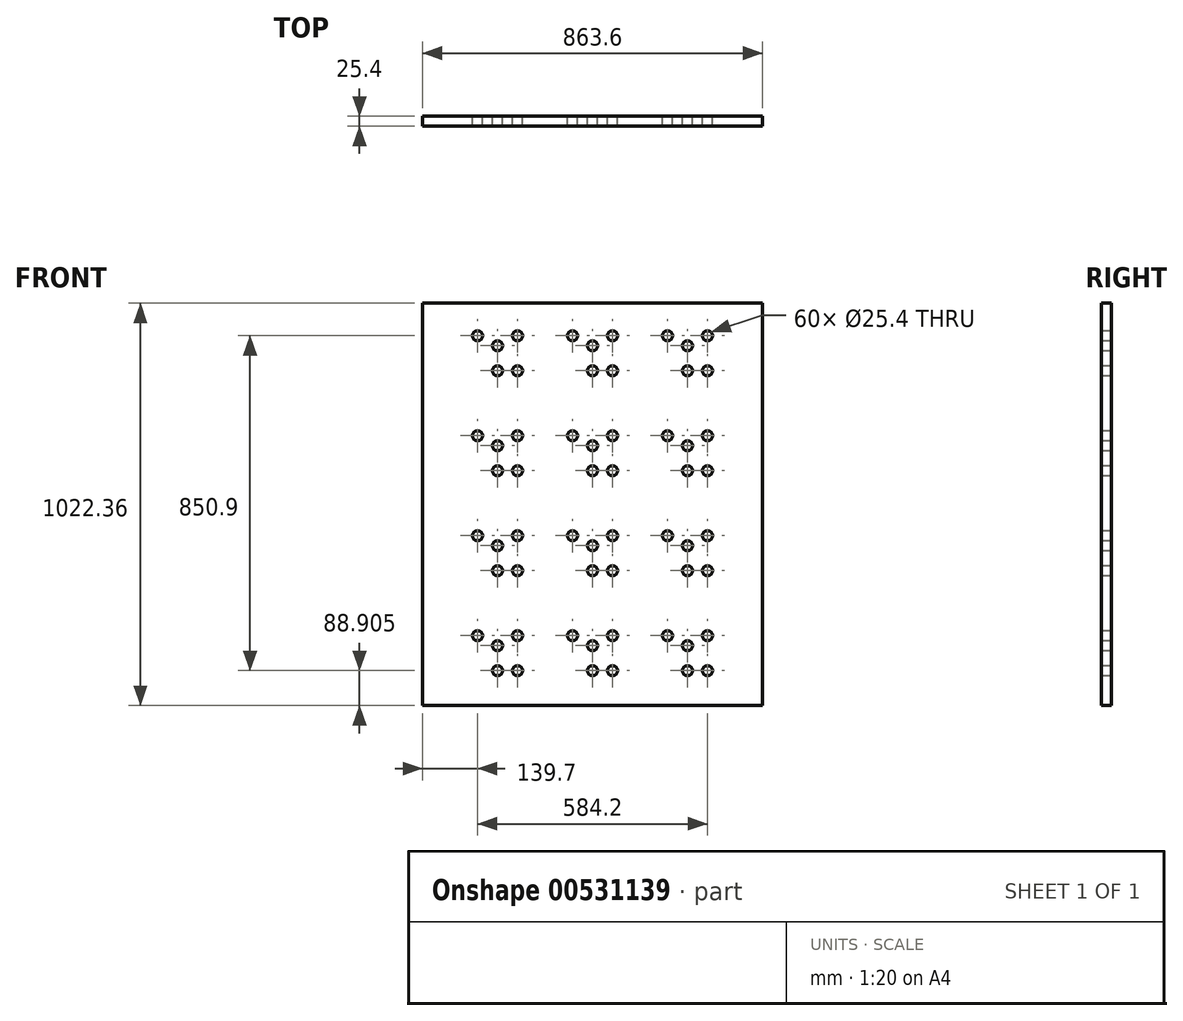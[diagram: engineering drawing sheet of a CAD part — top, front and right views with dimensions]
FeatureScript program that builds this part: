
annotation { "Feature Type Name" : "Feature", "Feature Type Description" : "" }
export const myFeature = defineFeature(function(context is Context, id is Id, definition is map)
    precondition{}
    {
        {
            var Q0;
            Q0=qCreatedBy(makeId("Front.planeOp"),FACE);
            var sketch = newSketch(context, id + "F0", { "sketchPlane" : qUnion([Q0])});
            skLineSegment(sketch, "E0.bottom", {"start": v(431.8, 511.18) * mm, "end": v(-431.8, 511.18) * mm});
            skLineSegment(sketch, "E0.top", {"start": v(431.8, -511.18) * mm, "end": v(-431.8, -511.18) * mm});
            skLineSegment(sketch, "E0.left", {"start": v(431.8, 511.18) * mm, "end": v(431.8, -511.18) * mm});
            skLineSegment(sketch, "E0.right", {"start": v(-431.8, 511.18) * mm, "end": v(-431.8, -511.18) * mm});
            skPoint(sketch, "E0.middle", {"position": v(0, 0) * mm});
            skCircle(sketch, "E1", {"center": v(-292.1, 428.63) * mm, "radius": 12.7 * mm});
            skCircle(sketch, "E2", {"center": v(-241.3, 403.23) * mm, "radius": 12.7 * mm});
            skCircle(sketch, "E3", {"center": v(-241.3, 339.73) * mm, "radius": 12.7 * mm});
            skCircle(sketch, "E4", {"center": v(-190.5, 339.73) * mm, "radius": 12.7 * mm});
            skCircle(sketch, "E5", {"center": v(-190.5, 428.63) * mm, "radius": 12.7 * mm});
            skCircle(sketch, "E6.0.1.0", {"center": v(-190.5, 85.73) * mm, "radius": 12.7 * mm});
            skCircle(sketch, "E6.0.1.1", {"center": v(-190.5, 174.63) * mm, "radius": 12.7 * mm});
            skCircle(sketch, "E6.0.1.2", {"center": v(-241.3, 149.23) * mm, "radius": 12.7 * mm});
            skCircle(sketch, "E6.0.1.3", {"center": v(-241.3, 85.73) * mm, "radius": 12.7 * mm});
            skCircle(sketch, "E6.0.1.4", {"center": v(-292.1, 174.63) * mm, "radius": 12.7 * mm});
            skCircle(sketch, "E6.0.2.0", {"center": v(-190.5, -168.27) * mm, "radius": 12.7 * mm});
            skCircle(sketch, "E6.0.2.1", {"center": v(-190.5, -79.37) * mm, "radius": 12.7 * mm});
            skCircle(sketch, "E6.0.2.2", {"center": v(-241.3, -104.77) * mm, "radius": 12.7 * mm});
            skCircle(sketch, "E6.0.2.3", {"center": v(-241.3, -168.27) * mm, "radius": 12.7 * mm});
            skCircle(sketch, "E6.0.2.4", {"center": v(-292.1, -79.37) * mm, "radius": 12.7 * mm});
            skCircle(sketch, "E6.0.3.0", {"center": v(-190.5, -422.27) * mm, "radius": 12.7 * mm});
            skCircle(sketch, "E6.0.3.1", {"center": v(-190.5, -333.38) * mm, "radius": 12.7 * mm});
            skCircle(sketch, "E6.0.3.2", {"center": v(-241.3, -358.77) * mm, "radius": 12.7 * mm});
            skCircle(sketch, "E6.0.3.3", {"center": v(-241.3, -422.27) * mm, "radius": 12.7 * mm});
            skCircle(sketch, "E6.0.3.4", {"center": v(-292.1, -333.38) * mm, "radius": 12.7 * mm});
            skCircle(sketch, "E6.1.0.0", {"center": v(50.8, 339.73) * mm, "radius": 12.7 * mm});
            skCircle(sketch, "E6.1.0.1", {"center": v(50.8, 428.63) * mm, "radius": 12.7 * mm});
            skCircle(sketch, "E6.1.0.2", {"center": v(0, 403.23) * mm, "radius": 12.7 * mm});
            skCircle(sketch, "E6.1.0.3", {"center": v(0, 339.73) * mm, "radius": 12.7 * mm});
            skCircle(sketch, "E6.1.0.4", {"center": v(-50.8, 428.63) * mm, "radius": 12.7 * mm});
            skCircle(sketch, "E6.1.1.0", {"center": v(50.8, 85.73) * mm, "radius": 12.7 * mm});
            skCircle(sketch, "E6.1.1.1", {"center": v(50.8, 174.63) * mm, "radius": 12.7 * mm});
            skCircle(sketch, "E6.1.1.2", {"center": v(0, 149.23) * mm, "radius": 12.7 * mm});
            skCircle(sketch, "E6.1.1.3", {"center": v(0, 85.73) * mm, "radius": 12.7 * mm});
            skCircle(sketch, "E6.1.1.4", {"center": v(-50.8, 174.63) * mm, "radius": 12.7 * mm});
            skCircle(sketch, "E6.1.2.0", {"center": v(50.8, -168.27) * mm, "radius": 12.7 * mm});
            skCircle(sketch, "E6.1.2.1", {"center": v(50.8, -79.37) * mm, "radius": 12.7 * mm});
            skCircle(sketch, "E6.1.2.2", {"center": v(0, -104.77) * mm, "radius": 12.7 * mm});
            skCircle(sketch, "E6.1.2.3", {"center": v(0, -168.27) * mm, "radius": 12.7 * mm});
            skCircle(sketch, "E6.1.2.4", {"center": v(-50.8, -79.37) * mm, "radius": 12.7 * mm});
            skCircle(sketch, "E6.1.3.0", {"center": v(50.8, -422.27) * mm, "radius": 12.7 * mm});
            skCircle(sketch, "E6.1.3.1", {"center": v(50.8, -333.38) * mm, "radius": 12.7 * mm});
            skCircle(sketch, "E6.1.3.2", {"center": v(0, -358.77) * mm, "radius": 12.7 * mm});
            skCircle(sketch, "E6.1.3.3", {"center": v(0, -422.27) * mm, "radius": 12.7 * mm});
            skCircle(sketch, "E6.1.3.4", {"center": v(-50.8, -333.38) * mm, "radius": 12.7 * mm});
            skCircle(sketch, "E6.2.0.0", {"center": v(292.1, 339.73) * mm, "radius": 12.7 * mm});
            skCircle(sketch, "E6.2.0.1", {"center": v(292.1, 428.63) * mm, "radius": 12.7 * mm});
            skCircle(sketch, "E6.2.0.2", {"center": v(241.3, 403.23) * mm, "radius": 12.7 * mm});
            skCircle(sketch, "E6.2.0.3", {"center": v(241.3, 339.73) * mm, "radius": 12.7 * mm});
            skCircle(sketch, "E6.2.0.4", {"center": v(190.5, 428.63) * mm, "radius": 12.7 * mm});
            skCircle(sketch, "E6.2.1.0", {"center": v(292.1, 85.73) * mm, "radius": 12.7 * mm});
            skCircle(sketch, "E6.2.1.1", {"center": v(292.1, 174.63) * mm, "radius": 12.7 * mm});
            skCircle(sketch, "E6.2.1.2", {"center": v(241.3, 149.23) * mm, "radius": 12.7 * mm});
            skCircle(sketch, "E6.2.1.3", {"center": v(241.3, 85.73) * mm, "radius": 12.7 * mm});
            skCircle(sketch, "E6.2.1.4", {"center": v(190.5, 174.63) * mm, "radius": 12.7 * mm});
            skCircle(sketch, "E6.2.2.0", {"center": v(292.1, -168.27) * mm, "radius": 12.7 * mm});
            skCircle(sketch, "E6.2.2.1", {"center": v(292.1, -79.37) * mm, "radius": 12.7 * mm});
            skCircle(sketch, "E6.2.2.2", {"center": v(241.3, -104.77) * mm, "radius": 12.7 * mm});
            skCircle(sketch, "E6.2.2.3", {"center": v(241.3, -168.27) * mm, "radius": 12.7 * mm});
            skCircle(sketch, "E6.2.2.4", {"center": v(190.5, -79.37) * mm, "radius": 12.7 * mm});
            skCircle(sketch, "E6.2.3.0", {"center": v(292.1, -422.27) * mm, "radius": 12.7 * mm});
            skCircle(sketch, "E6.2.3.1", {"center": v(292.1, -333.38) * mm, "radius": 12.7 * mm});
            skCircle(sketch, "E6.2.3.2", {"center": v(241.3, -358.77) * mm, "radius": 12.7 * mm});
            skCircle(sketch, "E6.2.3.3", {"center": v(241.3, -422.27) * mm, "radius": 12.7 * mm});
            skCircle(sketch, "E6.2.3.4", {"center": v(190.5, -333.38) * mm, "radius": 12.7 * mm});
            skLineSegment(sketch, "E6.direction1", {"start": v(-292.1, 428.63) * mm, "end": v(-50.8, 428.63) * mm, "construction": true});
            skLineSegment(sketch, "E6.direction2", {"start": v(-292.1, 428.63) * mm, "end": v(-292.1, 174.63) * mm, "construction": true});
            skSolve(sketch);
        }
        {
            var Q0;
            Q0 = qSketchRegion(id + "F0", true);
            extrude(context, id + "F1", {"entities" : qUnion([Q0]), "depth" : 25.4 * mm, "offsetDistance" : 25.4 * mm});
        }
    });
